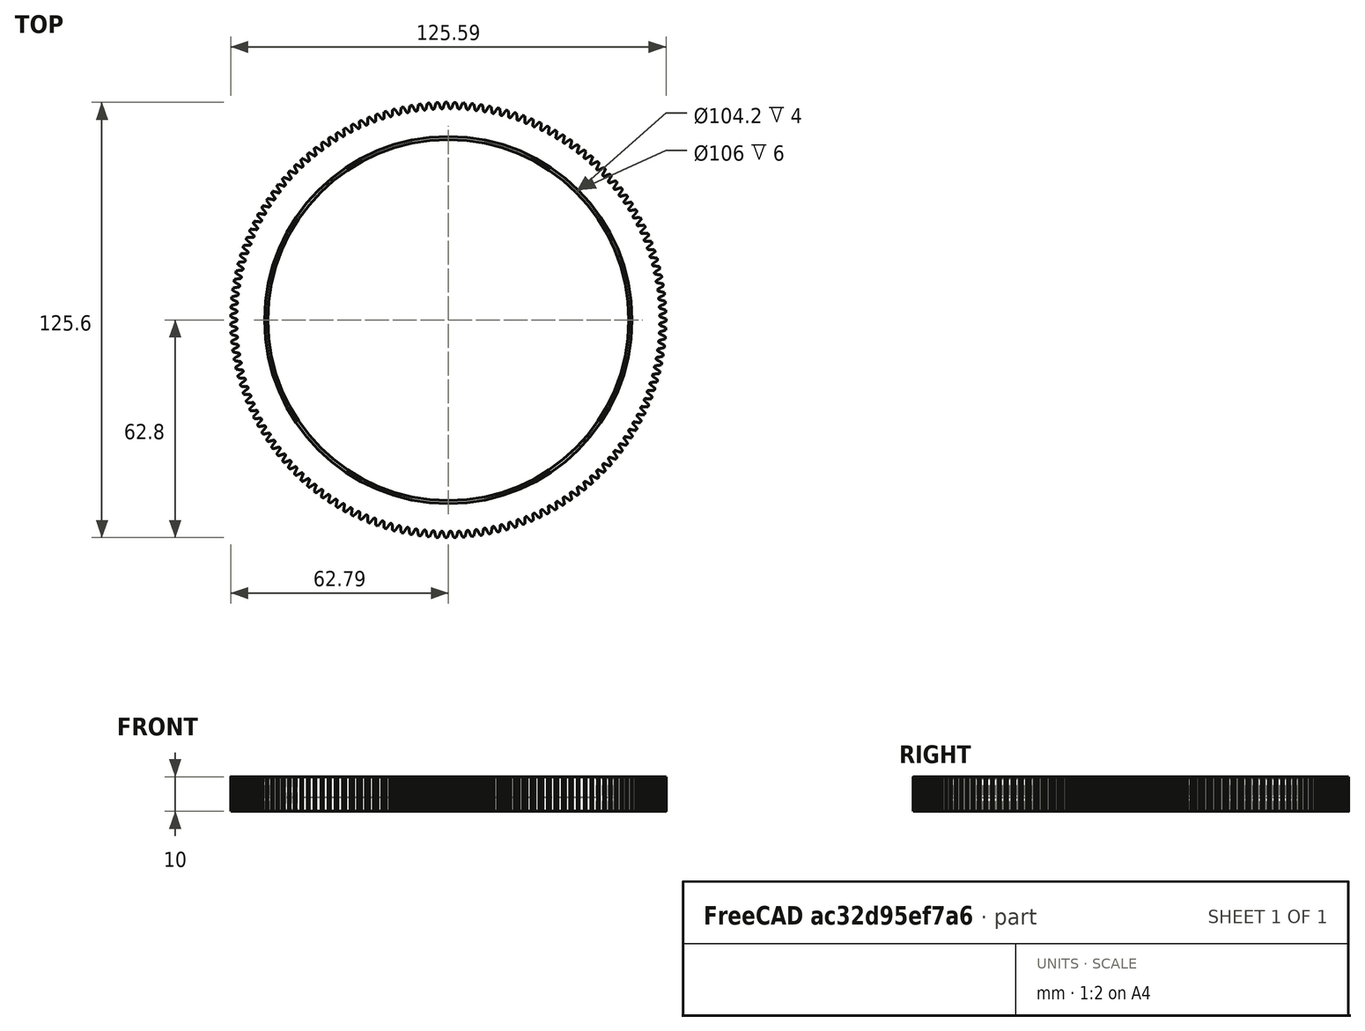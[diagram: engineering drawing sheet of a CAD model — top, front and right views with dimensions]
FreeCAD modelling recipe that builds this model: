
FCSTD DOCUMENT  (FreeCAD 0.17R13541 (Git))
Label: lomo-anamorphic-primes-ff
License: All rights reserved
LicenseURL: http://en.wikipedia.org/wiki/All_rights_reserved
objects: Drawing::FeatureViewPart×3, Part::Cylinder×2, Part::Cut×2, Part::Part2DObjectPython×1, PartDesign::Pad×1, Drawing::FeaturePage×1
note: 7 computed .brp shape members not serialized (recipe doc carries the construction recipe); baked Part::Feature solids carry a one-line shape summary decoded from their .brp

FEATURE [Part::Part2DObjectPython] InvoluteGear  # Draft 2D object (typed FeaturePython)
  ExternalGear = true
  HighPrecision = true
  MapMode = 5
  Modules = 0.8
  NumberOfTeeth = 155
  PressureAngle = 20
FEATURE [PartDesign::Pad] Pad
  Length = 10
  Length2 = 100
  Profile = -> InvoluteGear
  Type = 0
FEATURE [Part::Cylinder] Cylinder
  Angle = 360
  AttacherType = Attacher::AttachEngine3D
  Height = 10
  Radius = 52.1
FEATURE [Part::Cut] Cut  label="Gear"
  Base = -> Pad
  Tool = -> Cylinder
FEATURE [Part::Cylinder] Cylinder001
  Angle = 360
  AttacherType = Attacher::AttachEngine3D
  Height = 10
  Placement = pos=(0,0,4) rot=(0,0,1;0rad)
  Radius = 53
FEATURE [Part::Cut] Cut001  label="Final"
  Base = -> Cut
  Tool = -> Cylinder001
FEATURE [Drawing::FeatureViewPart] topView
  Direction = (0,0,1)
  HiddenWidth = 0.15
  LineWidth = 0.35
  Rotation = 180
  ShowHiddenLines = true
  ShowSmoothLines = false
  Source = -> Cut001
  Tolerance = 0.05
  ViewResult = <blob: 178807 chars omitted>
  Visible = false
  X = 115
  Y = 130
FEATURE [Drawing::FeatureViewPart] RightView
  Direction = (1,0,0)
  HiddenWidth = 0.15
  LineWidth = 0.35
  Rotation = 0
  ShowHiddenLines = true
  ShowSmoothLines = false
  Source = -> Cut001
  Tolerance = 0.05
  ViewResult = <blob: 207674 chars omitted>
  Visible = false
  X = 225
  Y = 130
FEATURE [Drawing::FeatureViewPart] IsoView
  Direction = (1,1,1)
  HiddenWidth = 0.15
  LineWidth = 0.35
  Rotation = 60
  ShowHiddenLines = true
  ShowSmoothLines = false
  Source = -> Cut001
  Tolerance = 0.05
  ViewResult = <blob: 299350 chars omitted>
  Visible = false
  X = 330
  Y = 130
FEATURE [Drawing::FeaturePage] AutoDrawing  label="Drawing"
  EditableTexts = FLOYD DIEBEL | 11/19/2018 | 1:1 | 1 | LOMO FOCUS GEAR | FOR 50mm and 75mm Anamorphic Lenses
  Group = -> [topView,RightView,IsoView]
  Template = C:/Program Files/FreeCAD 0.17/data/Mod/Drawing/Templates/A3_Landscape.svg
